# Revit family: IS_Edge_A7110_BIM_FR
name_source: partatom
category: Plumbing Fixtures
revit_build: Autodesk Revit 2017 (Build: 20160225_1515(x64)
units: mm (PartAtom-declared; Revit-internal decimal feet)

## family parameters
Always vertical = No
Cut with Voids When Loaded = No
OmniClass Number = 23.45.55.17
OmniClass Title = Mixing Faucets
Part Type = Normal
Room Calculation Point = No
Round Connector Dimension = Use Diameter
Shared = No
Work Plane-Based = No

## types (1)
- A7110AA - EDGE BSN MXR SLM HGH/SPT 5LPM PU/M
    Accessoires = www.idealstandard.be
    Auteur = Ideal Standard
    BOSUseNativeGeometries = 1
    Bim-NomDuProjet = ISI_IdealStandard_
    Caractéristiques = MELANGEUR DE LAVAGE DE BORD ROBINET SLM HGH / SPT 5LPM PU / M
    CodeBarre = 4015413343800
    ConseilsDInstallation = www.idealstandard.be
    Cost = 0 $
    Couleur = Chrome
    CoûtDeRemplacement = 0
    DateDeCréation = 2018_08_15
    Description = MELANGEUR DE LAVAGE DE BORD ROBINET SLM HGH / SPT 5LPM PU / M
    Dimensions = 96 x 193 x 248 mm
    Espace = Interne
    Finition = Chrome
    Forme = Complexe
    Hauteur = 248 mm
    IfcExportAs = IfcValveType
    IfcExportType = FAUCET
    InformationsProduit = www.idealstandard.be
    Largeur = 96 mm
    LienUtile = www.idealstandard.be
    Longueur = 193 mm
    Manufacturer = www.idealstandard.be
    Marque = Ideal Standard
    Model = A7110AA
    PoidsNet = 2,12 KG
    PressionDeFonctionnement = 0
    PressionMaximum = 3 Bar
    Profondeur = 0 mm  [stored 0 ft]
    Raccordement = Plomberie
    Révision = 1
    TypeDeRobinetterie = Bassin de lavage et raccords d'alimentation en eau creux
    URL = www.idealstandard.be
    Uniclass2015Code = PR-35-79-95
    Uniclass2015Title = Wash Basin And Trough Water Supply Fittings
    Uniclass2015Version = Products v1.1
    UnitéDeMesure = Millimètres
    UnitéDeTemps = An
    UnitéMonétaire = €
    UrlDuFabricant = www.idealstandard.be
    UsageDeLaRobinetterie = Bassin de lavage et raccords d'alimentation en eau creux
    Version = 1

note: [stored X ft] marks values corroborated as IEEE doubles in the binary element streams (Revit-internal decimal feet)

## geometry (parser evidence)
native form markers: Sweep x1
no freeform markers — native parametric forms only
